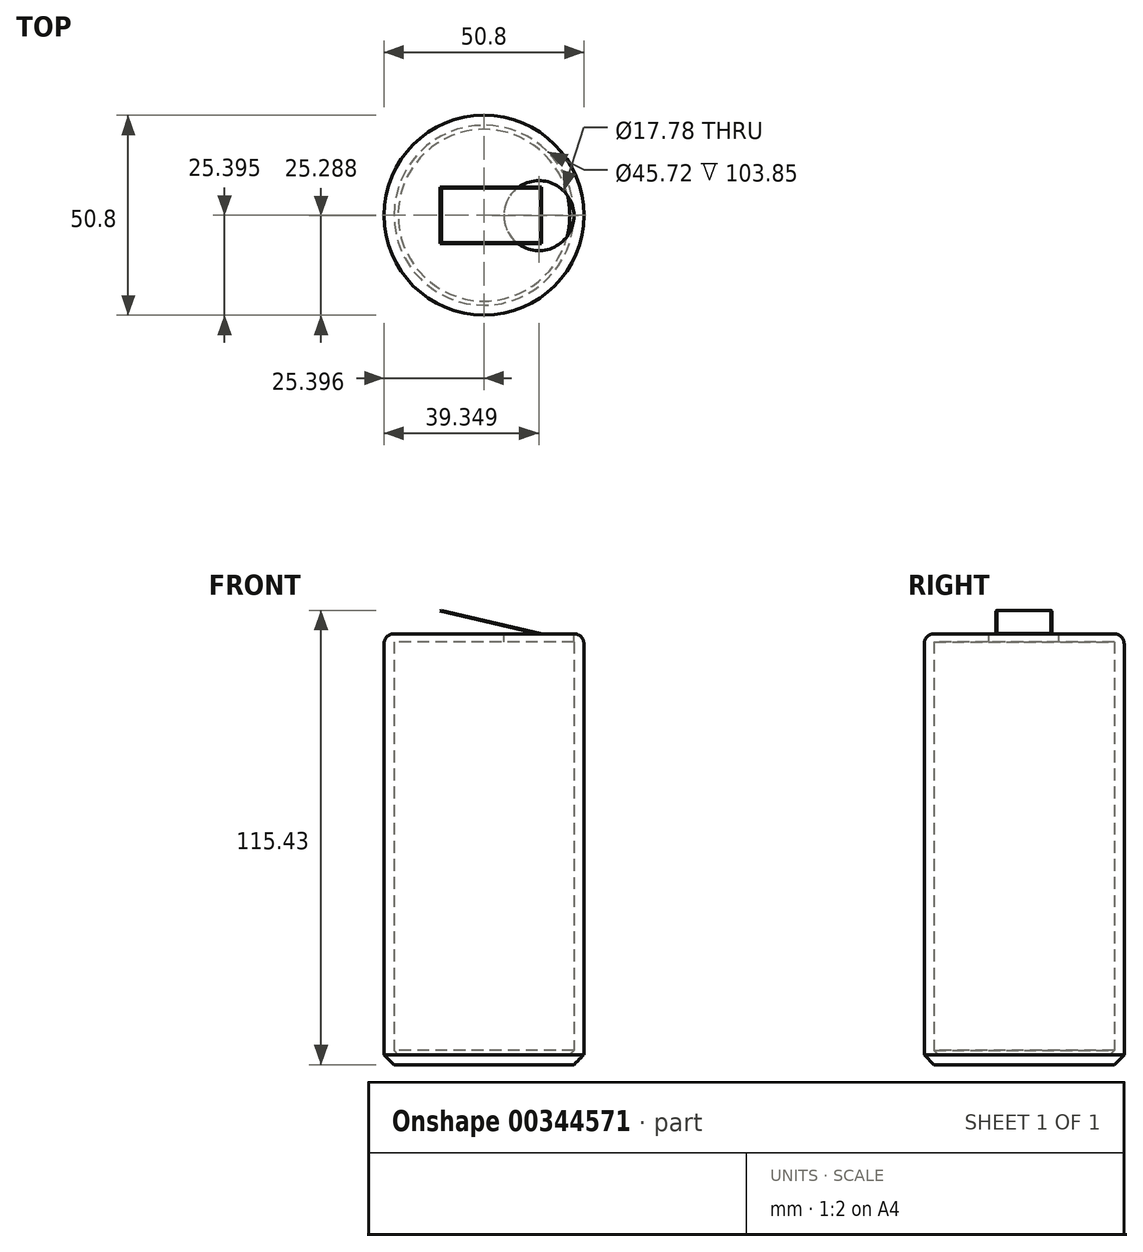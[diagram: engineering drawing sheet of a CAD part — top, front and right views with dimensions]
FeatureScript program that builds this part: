
annotation { "Feature Type Name" : "Feature", "Feature Type Description" : "" }
export const myFeature = defineFeature(function(context is Context, id is Id, definition is map)
    precondition{}
    {
        {
            var Q0;
            Q0=qCreatedBy(makeId("Top.planeOp"),FACE);
            var sketch = newSketch(context, id + "F0", { "sketchPlane" : qUnion([Q0])});
            skCircle(sketch, "E0", {"center": v(-105.93, 33.15) * mm, "radius": 25.4 * mm});
            skSolve(sketch);
        }
        {
            var Q0;
            Q0=makeQuery(id+"F0.imprint","IMPRINT",FACE,{"disambiguationData":[TD([[makeQuery(id+"F0.imprint","IMPRINT",EDGE,{"derivedFrom":sQuery(id+"F0.wireOp",EDGE,"E0")}),1.0]])]});
            extrude(context, id + "F1", {"entities" : qUnion([Q0]), "depth" : 107.44 * mm});
        }
        {
            var Q0;
            Q0=makeQuery(id+"F1.opExtrude","CAP_EDGE",EDGE,{"disambiguationData":[OSD([sQuery(id+"F0.wireOp",EDGE,"E0")])],"isStart":true});
            chamfer(context, id + "F2", {"entities" : qUnion([Q0]), "width" : 2.54 * mm, "tangentPropagation" : true});
        }
        {
            var Q0;
            Q0=makeQuery(id+"F1.opExtrude","CAP_FACE",FACE,{"disambiguationData":[OSD([sQuery(id+"F0.wireOp",EDGE,"E0")])],"isStart":false});
            shell(context, id + "F3", {"entities" : qUnion([Q0]), "thickness" : 2.54 * mm});
        }
        {
            var Q0;
            Q0=makeQuery(id+"F1.opExtrude","CAP_FACE",FACE,{"disambiguationData":[OSD([sQuery(id+"F0.wireOp",EDGE,"E0")])],"isStart":false});
            var sketch = newSketch(context, id + "F4", { "sketchPlane" : qUnion([Q0])});
            skCircle(sketch, "E1", {"center": v(-105.93, 33.15) * mm, "radius": 25.4 * mm});
            skSolve(sketch);
        }
        {
            var Q0;
            Q0 = qSketchRegion(id + "F4", true);
            extrude(context, id + "F5", {"entities" : qUnion([Q0]), "operationType" : NewBodyOperationType.ADD, "depth" : 2.03 * mm});
        }
        {
            var Q0;
            Q0=makeQuery(id+"F5.opExtrude","CAP_EDGE",EDGE,{"disambiguationData":[OSD([sQuery(id+"F4.wireOp",EDGE,"E1")])],"isStart":false});
            fillet(context, id + "F6", {"entities" : qUnion([Q0]), "radius" : 2.54 * mm, "tangentPropagation" : true, "allowEdgeOverflow" : false});
        }
        {
            var Q0;
            Q0=qCreatedBy(makeId("Top.planeOp"),FACE);
            var sketch = newSketch(context, id + "F7", { "sketchPlane" : qUnion([Q0])});
            skLineSegment(sketch, "E2", {"start": v(-111.29, -55.68) * mm, "end": v(-111.29, 102.37) * mm, "construction": true});
            skSolve(sketch);
        }
        {
            var Q0;
            Q0=qCreatedBy(makeId("Right.planeOp"),FACE);
            var Q1;
            Q1=sQuery(id+"F7.wireOp",EDGE,"E2");
            cPlane(context, id + "F8", {"entities" : qUnion([Q0, Q1]), "cplaneType" : CPlaneType.LINE_ANGLE, "offset" : 25.4 * mm, "angle" : 77.03 * degree, "oppositeDirection" : true, "width" : 152.4 * mm, "height" : 152.4 * mm});
        }
        {
            var Q0;
            Q0=qCreatedBy(id+"F8.planeOp",FACE);
            cPlane(context, id + "F9", {"entities" : qUnion([Q0]), "cplaneType" : CPlaneType.OFFSET, "offset" : 111 * mm, "oppositeDirection" : true, "width" : 152.4 * mm, "height" : 152.4 * mm});
        }
        {
            var Q0;
            Q0=qCreatedBy(id+"F9.planeOp",FACE);
            var sketch = newSketch(context, id + "F10", { "sketchPlane" : qUnion([Q0])});
            skLineSegment(sketch, "E3.bottom", {"start": v(-112.28, -24.7) * mm, "end": v(-141.22, -24.7) * mm});
            skLineSegment(sketch, "E3.top", {"start": v(-112.28, -41.53) * mm, "end": v(-141.22, -41.53) * mm});
            skLineSegment(sketch, "E3.left", {"start": v(-112.28, -24.7) * mm, "end": v(-112.28, -41.53) * mm});
            skLineSegment(sketch, "E3.right", {"start": v(-141.22, -24.7) * mm, "end": v(-141.22, -41.53) * mm});
            skSolve(sketch);
        }
        {
            var Q0;
            Q0=makeQuery(id+"F10.imprint","IMPRINT",FACE,{"disambiguationData":[TD([[makeQuery(id+"F10.imprint","IMPRINT",EDGE,{"derivedFrom":sQuery(id+"F10.wireOp",EDGE,"E3.bottom")}),1.0]])]});
            extrude(context, id + "F11", {"entities" : qUnion([Q0]), "oppositeDirection" : true, "depth" : 0.25 * mm});
        }
        {
            var Q0;
            Q0=makeQuery(id+"F5.opExtrude","CAP_FACE",FACE,{"disambiguationData":[OSD([sQuery(id+"F4.wireOp",EDGE,"E1")])],"isStart":false});
            var sketch = newSketch(context, id + "F12", { "sketchPlane" : qUnion([Q0])});
            skCircle(sketch, "E4", {"center": v(-91.98, 33.04) * mm, "radius": 8.9 * mm});
            skSolve(sketch);
        }
        {
            var Q0;
            Q0=sQuery(id+"F12.wireOp",VERTEX,"E4.center");
            var Q1;
            Q1=makeQuery(id+"F1.opExtrude","SWEPT_BODY",BODY,{"disambiguationData":[OSD([sQuery(id+"F0.wireOp",EDGE,"E0")])]});
            hole(context, id + "F13", {"style" : HoleStyle.SIMPLE, "endStyle" : HoleEndStyle.BLIND, "holeDiameter" : 17.78 * mm, "holeDepth" : 12.7 * mm, "isTappedThrough" : true, "tappedDepth" : 12.7 * mm, "tapClearance" : 3, "startFromSketch" : true, "locations" : qUnion([Q0]), "scope" : qUnion([Q1])});
        }
        {
            var Q0;
            Q0=makeQuery(id+"F11.opExtrude","CAP_EDGE",EDGE,{"disambiguationData":[OSD([sQuery(id+"F10.wireOp",EDGE,"E3.right")])],"isStart":false});
            var Q1;
            Q1=makeQuery(id+"F11.opExtrude","CAP_EDGE",EDGE,{"disambiguationData":[OSD([sQuery(id+"F10.wireOp",EDGE,"E3.top")])],"isStart":false});
            var Q2;
            Q2=makeQuery(id+"F11.opExtrude","CAP_EDGE",EDGE,{"disambiguationData":[OSD([sQuery(id+"F10.wireOp",EDGE,"E3.bottom")])],"isStart":false});
            var Q3;
            Q3=makeQuery(id+"F11.opExtrude","CAP_EDGE",EDGE,{"disambiguationData":[OSD([sQuery(id+"F10.wireOp",EDGE,"E3.left")])],"isStart":false});
            chamfer(context, id + "F14", {"entities" : qUnion([Q0, Q1, Q2, Q3]), "width" : 1.52 * mm, "tangentPropagation" : true});
        }
        {
            var Q0;
            Q0=qCreatedBy(makeId("Front.planeOp"),FACE);
            cPlane(context, id + "F15", {"entities" : qUnion([Q0]), "cplaneType" : CPlaneType.OFFSET, "offset" : 7.87 * mm, "oppositeDirection" : true, "width" : 152.4 * mm, "height" : 152.4 * mm});
        }
    });
